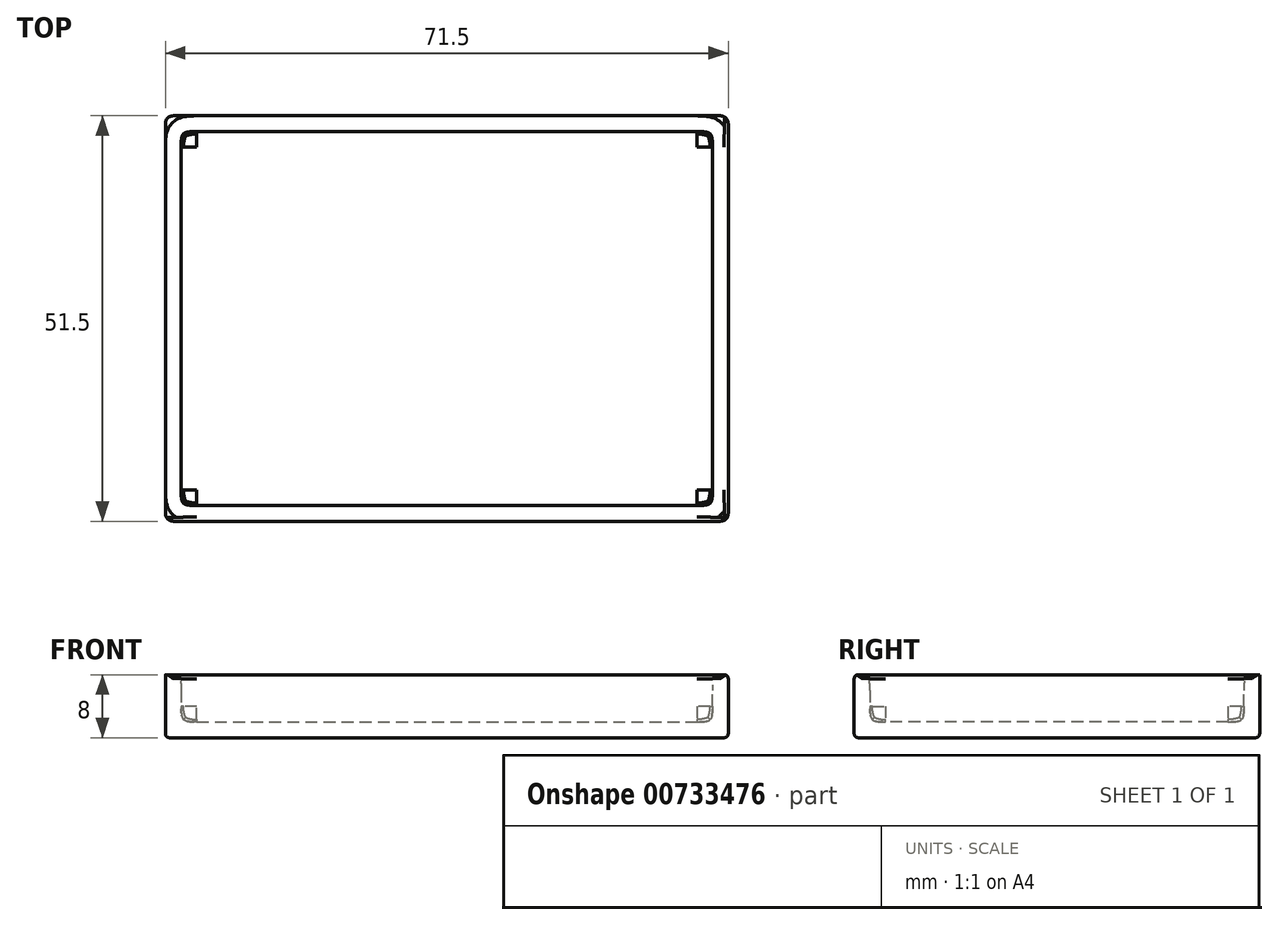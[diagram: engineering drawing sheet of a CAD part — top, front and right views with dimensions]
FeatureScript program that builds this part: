
annotation { "Feature Type Name" : "Feature", "Feature Type Description" : "" }
export const myFeature = defineFeature(function(context is Context, id is Id, definition is map)
    precondition{}
    {
        {
            var Q0;
            Q0=qCreatedBy(makeId("Top.planeOp"),FACE);
            var sketch = newSketch(context, id + "F0", { "sketchPlane" : qUnion([Q0])});
            skLineSegment(sketch, "E0.bottom", {"start": v(-35.75, 25.75) * mm, "end": v(35.75, 25.75) * mm});
            skLineSegment(sketch, "E0.top", {"start": v(-35.75, -25.75) * mm, "end": v(35.75, -25.75) * mm});
            skLineSegment(sketch, "E0.left", {"start": v(-35.75, 25.75) * mm, "end": v(-35.75, -25.75) * mm});
            skLineSegment(sketch, "E0.right", {"start": v(35.75, 25.75) * mm, "end": v(35.75, -25.75) * mm});
            skPoint(sketch, "E0.middle", {"position": v(0, 0) * mm});
            skSolve(sketch);
        }
        {
            var Q0;
            Q0=qSketchRegion(id+"F0",true);
            extrude(context, id + "F1", {"entities" : qUnion([Q0]), "depth" : 8 * mm, "offsetDistance" : 25 * mm, "symmetric" : true});
        }
        {
            var Q0;
            Q0=makeQuery(id+"F1.opExtrude","CAP_FACE",FACE,{"disambiguationData":[OSD([sQuery(id+"F0.wireOp",EDGE,"E0.bottom"),sQuery(id+"F0.wireOp",EDGE,"E0.top"),sQuery(id+"F0.wireOp",EDGE,"E0.left"),sQuery(id+"F0.wireOp",EDGE,"E0.right")])],"isStart":false});
            shell(context, id + "F2", {"entities" : qUnion([Q0]), "thickness" : 2 * mm});
        }
        {
            var Q0;
            {var subQ0=sQuery(id+"F0.wireOp",EDGE,"E0.top");Q0=makeQuery(id+"F2.opShell","OFFSET_EDGE",EDGE,{"disambiguationData":[OSD([subQ0]),TDD([makeQuery(id+"F1.opExtrude","CAP_EDGE",EDGE,{"disambiguationData":[OSD([subQ0])],"isStart":false})])]});}
            var Q1;
            Q1=makeQuery(id+"F2.opShell","OFFSET_FACE",FACE,{"disambiguationData":[OSD([sQuery(id+"F0.wireOp",EDGE,"E0.bottom"),sQuery(id+"F0.wireOp",EDGE,"E0.top"),sQuery(id+"F0.wireOp",EDGE,"E0.left"),sQuery(id+"F0.wireOp",EDGE,"E0.right")])]});
            var Q2;
            {var subQ0=sQuery(id+"F0.wireOp",EDGE,"E0.right");Q2=makeQuery(id+"F2.opShell","OFFSET_EDGE",EDGE,{"disambiguationData":[OSD([subQ0]),TDD([makeQuery(id+"F1.opExtrude","CAP_EDGE",EDGE,{"disambiguationData":[OSD([subQ0])],"isStart":false})])]});}
            var Q3;
            {var subQ0=sQuery(id+"F0.wireOp",EDGE,"E0.left");Q3=makeQuery(id+"F2.opShell","OFFSET_EDGE",EDGE,{"disambiguationData":[OSD([subQ0]),TDD([makeQuery(id+"F1.opExtrude","CAP_EDGE",EDGE,{"disambiguationData":[OSD([subQ0])],"isStart":false})])]});}
            var Q4;
            {var subQ0=sQuery(id+"F0.wireOp",EDGE,"E0.bottom");Q4=makeQuery(id+"F2.opShell","OFFSET_EDGE",EDGE,{"disambiguationData":[OSD([subQ0]),TDD([makeQuery(id+"F1.opExtrude","CAP_EDGE",EDGE,{"disambiguationData":[OSD([subQ0])],"isStart":false})])]});}
            var Q5;
            Q5=makeQuery(id+"F2.opShell","OFFSET_EDGE",EDGE,{"disambiguationData":[OSD([sQuery(id+"F0.wireOp",EDGE,"E0.top"),sQuery(id+"F0.wireOp",EDGE,"E0.right")])]});
            var Q6;
            Q6=makeQuery(id+"F2.opShell","OFFSET_EDGE",EDGE,{"disambiguationData":[OSD([sQuery(id+"F0.wireOp",EDGE,"E0.bottom"),sQuery(id+"F0.wireOp",EDGE,"E0.right")])]});
            var Q7;
            Q7=makeQuery(id+"F2.opShell","OFFSET_EDGE",EDGE,{"disambiguationData":[OSD([sQuery(id+"F0.wireOp",EDGE,"E0.top"),sQuery(id+"F0.wireOp",EDGE,"E0.left")])]});
            var Q8;
            Q8=makeQuery(id+"F2.opShell","OFFSET_EDGE",EDGE,{"disambiguationData":[OSD([sQuery(id+"F0.wireOp",EDGE,"E0.bottom"),sQuery(id+"F0.wireOp",EDGE,"E0.left")])]});
            fillet(context, id + "F3", {"entities" : qUnion([Q0, Q1, Q2, Q3, Q4, Q5, Q6, Q7, Q8]), "radius" : 2 * mm, "tangentPropagation" : true, "rho" : 0.7, "crossSection" : FilletCrossSection.CONIC, "allowEdgeOverflow" : false});
        }
        {
            var Q0;
            Q0=makeQuery(id+"F1.opExtrude","SWEPT_EDGE",EDGE,{"disambiguationData":[OSD([sQuery(id+"F0.wireOp",EDGE,"E0.top"),sQuery(id+"F0.wireOp",EDGE,"E0.left")])]});
            var Q1;
            Q1=makeQuery(id+"F1.opExtrude","SWEPT_EDGE",EDGE,{"disambiguationData":[OSD([sQuery(id+"F0.wireOp",EDGE,"E0.bottom"),sQuery(id+"F0.wireOp",EDGE,"E0.left")])]});
            var Q2;
            Q2=makeQuery(id+"F1.opExtrude","SWEPT_EDGE",EDGE,{"disambiguationData":[OSD([sQuery(id+"F0.wireOp",EDGE,"E0.bottom"),sQuery(id+"F0.wireOp",EDGE,"E0.right")])]});
            var Q3;
            Q3=makeQuery(id+"F1.opExtrude","SWEPT_EDGE",EDGE,{"disambiguationData":[OSD([sQuery(id+"F0.wireOp",EDGE,"E0.top"),sQuery(id+"F0.wireOp",EDGE,"E0.right")])]});
            fillet(context, id + "F4", {"entities" : qUnion([Q0, Q1, Q2, Q3]), "radius" : 1 * mm, "tangentPropagation" : true, "allowEdgeOverflow" : false});
        }
        {
            var Q0;
            Q0=makeQuery(id+"F1.opExtrude","CAP_EDGE",EDGE,{"disambiguationData":[OSD([sQuery(id+"F0.wireOp",EDGE,"E0.top")])],"isStart":true});
            var Q1;
            {var subQ0=sQuery(id+"F0.wireOp",EDGE,"E0.top");Q1=makeQuery(id+"F3.opFillet","BLEND_EDGE",EDGE,{"blendedFrom":[makeQuery(id+"F2.opShell","OFFSET_EDGE",EDGE,{"disambiguationData":[OSD([subQ0]),TDD([makeQuery(id+"F1.opExtrude","CAP_EDGE",EDGE,{"disambiguationData":[OSD([subQ0])],"isStart":false})])]}),makeQuery(id+"F1.opExtrude","SWEPT_FACE",FACE,{"disambiguationData":[OSD([subQ0])]})],"blendedInto":[makeQuery(id+"F1.opExtrude","SWEPT_FACE",FACE,{"disambiguationData":[OSD([subQ0])]})]});}
            var Q2;
            {var subQ0=sQuery(id+"F0.wireOp",EDGE,"E0.right");Q2=makeQuery(id+"F3.opFillet","BLEND_EDGE",EDGE,{"blendedFrom":[makeQuery(id+"F2.opShell","OFFSET_EDGE",EDGE,{"disambiguationData":[OSD([subQ0]),TDD([makeQuery(id+"F1.opExtrude","CAP_EDGE",EDGE,{"disambiguationData":[OSD([subQ0])],"isStart":false})])]}),makeQuery(id+"F1.opExtrude","SWEPT_FACE",FACE,{"disambiguationData":[OSD([subQ0])]})],"blendedInto":[makeQuery(id+"F1.opExtrude","SWEPT_FACE",FACE,{"disambiguationData":[OSD([subQ0])]})]});}
            var Q3;
            Q3=makeQuery(id+"F2.opShell","OFFSET_FACE",FACE,{"disambiguationData":[OSD([sQuery(id+"F0.wireOp",EDGE,"E0.bottom"),sQuery(id+"F0.wireOp",EDGE,"E0.top"),sQuery(id+"F0.wireOp",EDGE,"E0.left"),sQuery(id+"F0.wireOp",EDGE,"E0.right")])]});
            var Q4;
            Q4=makeQuery(id+"F1.opExtrude","CAP_FACE",FACE,{"disambiguationData":[OSD([sQuery(id+"F0.wireOp",EDGE,"E0.bottom"),sQuery(id+"F0.wireOp",EDGE,"E0.top"),sQuery(id+"F0.wireOp",EDGE,"E0.left"),sQuery(id+"F0.wireOp",EDGE,"E0.right")])],"isStart":true});
            fillet(context, id + "F5", {"entities" : qUnion([Q0, Q1, Q2, Q3, Q4]), "radius" : 0.5 * mm, "tangentPropagation" : true, "allowEdgeOverflow" : false});
        }
    });
